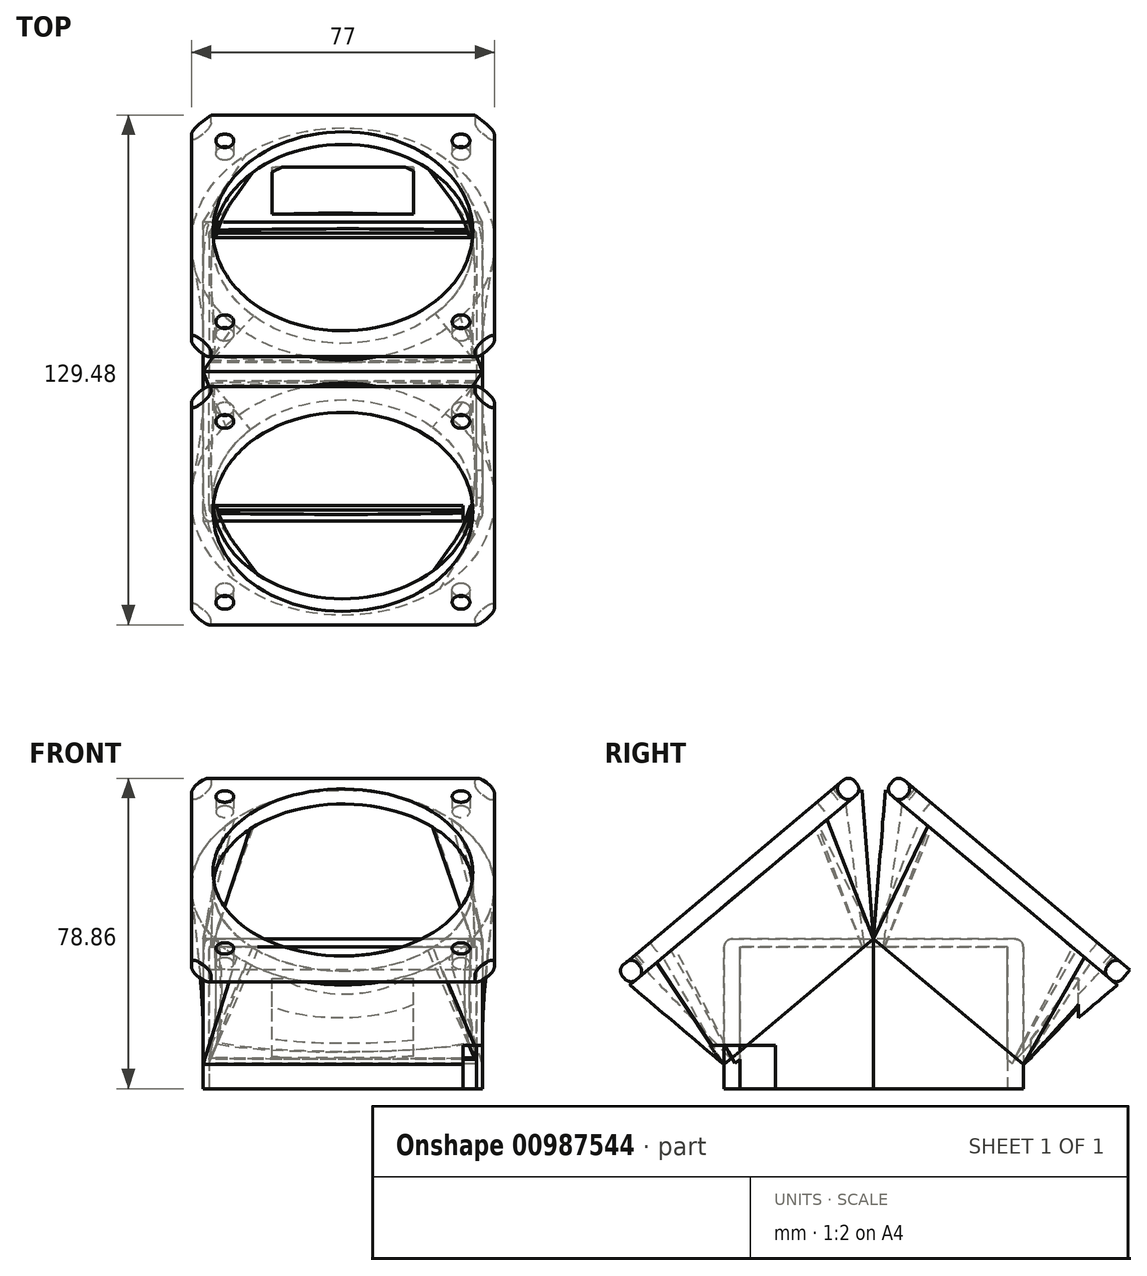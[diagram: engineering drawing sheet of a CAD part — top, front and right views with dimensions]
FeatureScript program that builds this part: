
annotation { "Feature Type Name" : "Feature", "Feature Type Description" : "" }
export const myFeature = defineFeature(function(context is Context, id is Id, definition is map)
    precondition{}
    {
        {
            var Q0;
            Q0=qCreatedBy(makeId("Front.planeOp"),FACE);
            var sketch = newSketch(context, id + "F0", { "sketchPlane" : qUnion([Q0])});
            skLineSegment(sketch, "E0.bottom", {"start": v(-34, 18) * mm, "end": v(34, 18) * mm});
            skLineSegment(sketch, "E0.top", {"start": v(-34, -18) * mm, "end": v(34, -18) * mm});
            skLineSegment(sketch, "E0.left", {"start": v(-34, 18) * mm, "end": v(-34, -18) * mm});
            skLineSegment(sketch, "E0.right", {"start": v(34, 18) * mm, "end": v(34, -18) * mm});
            skPoint(sketch, "E0.middle", {"position": v(0, 0) * mm});
            skSolve(sketch);
        }
        {
            var Q0;
            Q0=makeQuery(id+"F0.imprint","IMPRINT",FACE,{"disambiguationData":[TD([[makeQuery(id+"F0.imprint","IMPRINT",EDGE,{"derivedFrom":sQuery(id+"F0.wireOp",EDGE,"E0.bottom")}),-1.0]])]});
            extrude(context, id + "F1", {"entities" : qUnion([Q0]), "depth" : 34 * mm, "offsetDistance" : 25 * mm});
        }
        {
            var Q0;
            Q0=makeQuery(id+"F0.imprint","IMPRINT",FACE,{"disambiguationData":[TD([[makeQuery(id+"F0.imprint","IMPRINT",EDGE,{"derivedFrom":sQuery(id+"F0.wireOp",EDGE,"E0.bottom")}),-1.0]])]});
            var sketch = newSketch(context, id + "F2", { "sketchPlane" : qUnion([Q0])});
            skLineSegment(sketch, "E1", {"start": v(0, 18) * mm, "end": v(0, -18) * mm, "construction": true});
            skSolve(sketch);
        }
        {
            var Q0;
            Q0=sQuery(id+"F0.wireOp",EDGE,"E0.top");
            cPlane(context, id + "F3", {"entities" : qUnion([Q0]), "cplaneType" : CPlaneType.LINE_ANGLE, "offset" : 25 * mm, "angle" : 50 * degree, "oppositeDirection" : true, "width" : 150 * mm, "height" : 150 * mm});
        }
        {
            var Q0;
            Q0=sQuery(id+"F0.wireOp",EDGE,"E0.bottom");
            var Q1;
            Q1=qBodyType(qCreatedBy(id+"F5",EDGE),BodyType.WIRE);
            cPlane(context, id + "F4", {"entities" : qUnion([Q0, Q1]), "cplaneType" : CPlaneType.LINE_ANGLE, "offset" : 25 * mm, "angle" : 50 * degree, "oppositeDirection" : true, "width" : 150 * mm, "height" : 150 * mm});
        }
        {
            var Q0;
            Q0=qCreatedBy(id+"F4.planeOp",FACE);
            var sketch = newSketch(context, id + "F5", { "sketchPlane" : qUnion([Q0])});
            skLineSegment(sketch, "E2.bottom", {"start": v(34, -8.77) * mm, "end": v(-34, -8.77) * mm});
            skLineSegment(sketch, "E2.top", {"start": v(34, 34.4) * mm, "end": v(-34, 34.4) * mm});
            skLineSegment(sketch, "E2.left", {"start": v(34, -8.77) * mm, "end": v(34, 34.4) * mm});
            skLineSegment(sketch, "E2.right", {"start": v(-34, -8.77) * mm, "end": v(-34, 34.4) * mm});
            skSolve(sketch);
        }
        {
            var Q0;
            Q0=qCreatedBy(id+"F3.planeOp",FACE);
            cPlane(context, id + "F6", {"entities" : qUnion([Q0]), "cplaneType" : CPlaneType.OFFSET, "offset" : 60 * mm, "oppositeDirection" : true, "width" : 150 * mm, "height" : 150 * mm});
        }
        {
            var Q0;
            Q0=qCreatedBy(id+"F6.planeOp",FACE);
            var sketch = newSketch(context, id + "F7", { "sketchPlane" : qUnion([Q0])});
            skArc(sketch, "E3", {"start": v(22.98, 27.26) * mm, "mid": v(0.9, 36.56) * mm, "end": v(-21.64, 28.48) * mm});
            skArc(sketch, "E4", {"start": v(-21.64, 28.48) * mm, "mid": v(-32.97, 4.87) * mm, "end": v(-23.53, -19.57) * mm});
            skArc(sketch, "E5", {"start": v(-23.53, -19.57) * mm, "mid": v(-0.57, -29.42) * mm, "end": v(22.72, -20.36) * mm});
            skArc(sketch, "E6", {"start": v(22.72, -20.36) * mm, "mid": v(33, 3.4) * mm, "end": v(22.98, 27.26) * mm});
            skSolve(sketch);
        }
        {
            var Q0;
            Q0=qSketchRegion(id+"F5",true);
            var Q1;
            Q1=makeQuery(id+"F7.imprint","IMPRINT",FACE,{"disambiguationData":[TD([[makeQuery(id+"F7.imprint","IMPRINT",EDGE,{"derivedFrom":sQuery(id+"F7.wireOp",EDGE,"E3")}),1.0]])]});
            loft(context, id + "F8", {"sheetProfilesArray" : [{ "sheetProfileEntities" : qUnion([Q0]) }, { "sheetProfileEntities" : qUnion([Q1]) }]});
        }
        {
            var Q0;
            Q0=makeQuery(id+"F2.imprint","IMPRINT",FACE,{"disambiguationData":[TD([[makeQuery(id+"F2.imprint","IMPRINT",EDGE,{"derivedFrom":makeQuery(id+"F0.imprint","IMPRINT",EDGE,{"derivedFrom":sQuery(id+"F0.wireOp",EDGE,"E0.bottom")})}),-1.0]])]});
            var sketch = newSketch(context, id + "F9", { "sketchPlane" : qUnion([Q0])});
            skLineSegment(sketch, "E7.bottom", {"start": v(35.5, 20) * mm, "end": v(-35.5, 20) * mm});
            skLineSegment(sketch, "E7.top", {"start": v(35.5, -18) * mm, "end": v(-35.5, -18) * mm});
            skLineSegment(sketch, "E7.left", {"start": v(35.5, 20) * mm, "end": v(35.5, -18) * mm});
            skLineSegment(sketch, "E7.right", {"start": v(-35.5, 20) * mm, "end": v(-35.5, -18) * mm});
            skPoint(sketch, "E7.middle", {"position": v(0, 0) * mm});
            skSolve(sketch);
        }
        {
            var Q0;
            Q0=qSketchRegion(id+"F9",true);
            extrude(context, id + "F10", {"entities" : qUnion([Q0]), "depth" : 38 * mm, "offsetDistance" : 25 * mm});
        }
        {
            var Q0;
            Q0=sQuery(id+"F9.wireOp",EDGE,"E7.bottom");
            cPlane(context, id + "F11", {"entities" : qUnion([Q0]), "cplaneType" : CPlaneType.LINE_ANGLE, "offset" : 25 * mm, "angle" : 50 * degree, "width" : 150 * mm, "height" : 150 * mm});
        }
        {
            var Q0;
            Q0=qCreatedBy(id+"F11.planeOp",FACE);
            var sketch = newSketch(context, id + "F12", { "sketchPlane" : qUnion([Q0])});
            skLineSegment(sketch, "E8.bottom", {"start": v(-35.5, 12.86) * mm, "end": v(35.5, 12.86) * mm});
            skLineSegment(sketch, "E8.top", {"start": v(-35.5, -36.75) * mm, "end": v(35.5, -36.75) * mm});
            skLineSegment(sketch, "E8.left", {"start": v(-35.5, 12.86) * mm, "end": v(-35.5, -36.75) * mm});
            skLineSegment(sketch, "E8.right", {"start": v(35.5, 12.86) * mm, "end": v(35.5, -36.75) * mm});
            skSolve(sketch);
        }
        {
            var Q0;
            Q0=qCreatedBy(id+"F6.planeOp",FACE);
            var sketch = newSketch(context, id + "F13", { "sketchPlane" : qUnion([Q0])});
            skArc(sketch, "E9", {"start": v(-29.82, -20.78) * mm, "mid": v(-1.7, -34.9) * mm, "end": v(27.55, -23.32) * mm});
            skArc(sketch, "E10", {"start": v(27.55, -23.32) * mm, "mid": v(38.44, 5.63) * mm, "end": v(24.51, 33.26) * mm});
            skArc(sketch, "E11", {"start": v(24.51, 33.26) * mm, "mid": v(-1.62, 42.04) * mm, "end": v(-26.92, 31.1) * mm});
            skArc(sketch, "E12", {"start": v(-26.92, 31.1) * mm, "mid": v(-38.44, 5.72) * mm, "end": v(-29.82, -20.78) * mm});
            skSolve(sketch);
        }
        {
            var Q0;
            Q0=qCreatedBy(id+"F6.planeOp",FACE);
            var sketch = newSketch(context, id + "F14", { "sketchPlane" : qUnion([Q0])});
            skLineSegment(sketch, "E13.bottom", {"start": v(-38.5, -34.93) * mm, "end": v(38.5, -34.93) * mm});
            skLineSegment(sketch, "E13.top", {"start": v(-38.5, 42.07) * mm, "end": v(38.5, 42.07) * mm});
            skLineSegment(sketch, "E13.left", {"start": v(-38.5, -34.93) * mm, "end": v(-38.5, 42.07) * mm});
            skLineSegment(sketch, "E13.right", {"start": v(38.5, -34.93) * mm, "end": v(38.5, 42.07) * mm});
            skPoint(sketch, "E13.middle", {"position": v(0, 3.57) * mm});
            skSolve(sketch);
        }
        {
            var Q0;
            Q0=qCreatedBy(id+"F6.planeOp",FACE);
            var sketch = newSketch(context, id + "F15", { "sketchPlane" : qUnion([Q0])});
            skLineSegment(sketch, "E14.bottom", {"start": v(-30, -26.43) * mm, "end": v(30, -26.43) * mm, "construction": true});
            skLineSegment(sketch, "E14.top", {"start": v(-30, 33.57) * mm, "end": v(30, 33.57) * mm, "construction": true});
            skLineSegment(sketch, "E14.left", {"start": v(-30, -26.43) * mm, "end": v(-30, 33.57) * mm, "construction": true});
            skLineSegment(sketch, "E14.right", {"start": v(30, -26.43) * mm, "end": v(30, 33.57) * mm, "construction": true});
            skPoint(sketch, "E14.middle", {"position": v(0, 3.57) * mm});
            skSolve(sketch);
        }
        {
            var Q0;
            Q0=qCreatedBy(id+"F6.planeOp",FACE);
            var sketch = newSketch(context, id + "F16", { "sketchPlane" : qUnion([Q0])});
            skCircle(sketch, "E15", {"center": v(30, -26.43) * mm, "radius": 2.25 * mm});
            skCircle(sketch, "E16", {"center": v(-30, -26.43) * mm, "radius": 2.25 * mm});
            skCircle(sketch, "E17", {"center": v(-30, 33.57) * mm, "radius": 2.25 * mm});
            skCircle(sketch, "E18", {"center": v(30, 33.57) * mm, "radius": 2.25 * mm});
            skSolve(sketch);
        }
        {
            var Q0;
            Q0=makeQuery(id+"F8.opLoft","CAP_FACE",FACE,{"disambiguationData":[OSD([makeQuery(id+"F7.imprint","IMPRINT",FACE,{"disambiguationData":[TD([[makeQuery(id+"F7.imprint","IMPRINT",EDGE,{"derivedFrom":sQuery(id+"F7.wireOp",EDGE,"E3")}),1.0]])]})])],"isStart":true});
            var Q1;
            Q1=makeQuery(id+"F16.imprint","IMPRINT",FACE,{"disambiguationData":[TD([[makeQuery(id+"F16.imprint","IMPRINT",EDGE,{"derivedFrom":sQuery(id+"F16.wireOp",EDGE,"E18")}),1.0]])]});
            var Q2;
            Q2=makeQuery(id+"F16.imprint","IMPRINT",FACE,{"disambiguationData":[TD([[makeQuery(id+"F16.imprint","IMPRINT",EDGE,{"derivedFrom":sQuery(id+"F16.wireOp",EDGE,"E17")}),1.0]])]});
            var Q3;
            Q3=makeQuery(id+"F16.imprint","IMPRINT",FACE,{"disambiguationData":[TD([[makeQuery(id+"F16.imprint","IMPRINT",EDGE,{"derivedFrom":sQuery(id+"F16.wireOp",EDGE,"E16")}),1.0]])]});
            var Q4;
            Q4=makeQuery(id+"F16.imprint","IMPRINT",FACE,{"disambiguationData":[TD([[makeQuery(id+"F16.imprint","IMPRINT",EDGE,{"derivedFrom":sQuery(id+"F16.wireOp",EDGE,"E15")}),1.0]])]});
            extrude(context, id + "F17", {"entities" : qUnion([Q0, Q1, Q2, Q3, Q4]), "depth" : 5 * mm, "offsetDistance" : 25 * mm});
        }
        {
            var Q0;
            Q0=makeQuery(id+"F12.imprint","IMPRINT",FACE,{"disambiguationData":[TD([[makeQuery(id+"F12.imprint","IMPRINT",EDGE,{"derivedFrom":sQuery(id+"F12.wireOp",EDGE,"E8.bottom")}),-1.0]])]});
            var Q1;
            Q1=qSketchRegion(id+"F13",true);
            loft(context, id + "F18", {"sheetProfilesArray" : [{ "sheetProfileEntities" : qUnion([Q0]) }, { "sheetProfileEntities" : qUnion([Q1]) }]});
        }
        {
            var Q0;
            Q0=makeQuery(id+"F14.imprint","IMPRINT",FACE,{"disambiguationData":[TD([[makeQuery(id+"F14.imprint","IMPRINT",EDGE,{"derivedFrom":sQuery(id+"F14.wireOp",EDGE,"E13.bottom")}),1.0]])]});
            extrude(context, id + "F19", {"entities" : qUnion([Q0]), "oppositeDirection" : true, "depth" : 5 * mm, "offsetDistance" : 25 * mm});
        }
        {
            var Q0;
            Q0=makeQuery(id+"F17.opExtrude","SWEPT_BODY",BODY,{"disambiguationData":[OSD([sQuery(id+"F16.wireOp",EDGE,"E18")])]});
            var Q1;
            Q1=makeQuery(id+"F17.opExtrude","SWEPT_BODY",BODY,{"disambiguationData":[OSD([sQuery(id+"F16.wireOp",EDGE,"E17")])]});
            var Q2;
            Q2=makeQuery(id+"F17.opExtrude","SWEPT_BODY",BODY,{"disambiguationData":[OSD([sQuery(id+"F16.wireOp",EDGE,"E16")])]});
            var Q3;
            Q3=makeQuery(id+"F17.opExtrude","SWEPT_BODY",BODY,{"disambiguationData":[OSD([sQuery(id+"F16.wireOp",EDGE,"E15")])]});
            var Q4;
            Q4=makeQuery(id+"F17.opExtrude","SWEPT_BODY",BODY,{"disambiguationData":[OSD([makeQuery(id+"F7.imprint","IMPRINT",FACE,{"disambiguationData":[TD([[makeQuery(id+"F7.imprint","IMPRINT",EDGE,{"derivedFrom":sQuery(id+"F7.wireOp",EDGE,"E3")}),1.0]])]})])]});
            var Q5;
            Q5=makeQuery(id+"F8.opLoft","SWEPT_BODY",BODY,{"disambiguationData":[OSD([makeQuery(id+"F5.imprint","IMPRINT",FACE,{"disambiguationData":[TD([[makeQuery(id+"F5.imprint","IMPRINT",EDGE,{"derivedFrom":sQuery(id+"F5.wireOp",EDGE,"sHmJ6Bm4-Lffu-TfJG-ELbj-xKBSEGzgKOYK.bottom")}),-1.0]])]}),makeQuery(id+"F7.imprint","IMPRINT",FACE,{"disambiguationData":[TD([[makeQuery(id+"F7.imprint","IMPRINT",EDGE,{"derivedFrom":sQuery(id+"F7.wireOp",EDGE,"E3")}),1.0]])]})])]});
            var Q6;
            Q6=makeQuery(id+"F1.opExtrude","SWEPT_BODY",BODY,{"disambiguationData":[OSD([sQuery(id+"F0.wireOp",EDGE,"E0.bottom"),sQuery(id+"F0.wireOp",EDGE,"E0.top"),sQuery(id+"F0.wireOp",EDGE,"E0.left"),sQuery(id+"F0.wireOp",EDGE,"E0.right")])]});
            var Q7;
            Q7=makeQuery(id+"F10.opExtrude","SWEPT_BODY",BODY,{"disambiguationData":[OSD([sQuery(id+"F9.wireOp",EDGE,"E7.bottom"),sQuery(id+"F9.wireOp",EDGE,"E7.top"),sQuery(id+"F9.wireOp",EDGE,"E7.left"),sQuery(id+"F9.wireOp",EDGE,"E7.right")])]});
            var Q8;
            Q8=makeQuery(id+"F18.opLoft","SWEPT_BODY",BODY,{"disambiguationData":[OSD([makeQuery(id+"F12.imprint","IMPRINT",FACE,{"disambiguationData":[TD([[makeQuery(id+"F12.imprint","IMPRINT",EDGE,{"derivedFrom":sQuery(id+"F12.wireOp",EDGE,"E8.bottom")}),-1.0]])]}),makeQuery(id+"F13.imprint","IMPRINT",FACE,{"disambiguationData":[TD([[makeQuery(id+"F13.imprint","IMPRINT",EDGE,{"derivedFrom":sQuery(id+"F13.wireOp",EDGE,"q23MTACi-eoCC-Vc5T-UU1i-hVDggLDGJppy")}),1.0]])]})])]});
            var Q9;
            Q9=makeQuery(id+"F19.opExtrude","SWEPT_BODY",BODY,{"disambiguationData":[OSD([sQuery(id+"F14.wireOp",EDGE,"E13.bottom"),sQuery(id+"F14.wireOp",EDGE,"E13.top"),sQuery(id+"F14.wireOp",EDGE,"E13.left"),sQuery(id+"F14.wireOp",EDGE,"E13.right")])]});
            booleanBodies(context, id + "F20", {"operationType" : BooleanOperationType.SUBTRACTION, "tools" : qUnion([Q0, Q1, Q2, Q3, Q4, Q5, Q6]), "targets" : qUnion([Q7, Q8, Q9])});
        }
        {
            var Q0;
            Q0=makeQuery(id+"F10.opExtrude","SWEPT_BODY",BODY,{"disambiguationData":[OSD([sQuery(id+"F9.wireOp",EDGE,"E7.bottom"),sQuery(id+"F9.wireOp",EDGE,"E7.top"),sQuery(id+"F9.wireOp",EDGE,"E7.left"),sQuery(id+"F9.wireOp",EDGE,"E7.right")])]});
            var Q1;
            Q1=sQuery(id+"F2.wireOp",EDGE,"E1");
            transform(context, id + "F21", {"entities" : qUnion([Q0]), "transformType" : TransformType.ROTATION, "transformAxis" : qUnion([Q1]), "angle" : 180 * degree, "makeCopy" : true});
        }
        {
            var Q0;
            Q0=makeQuery(id+"F18.opLoft","SWEPT_BODY",BODY,{"disambiguationData":[OSD([makeQuery(id+"F12.imprint","IMPRINT",FACE,{"disambiguationData":[TD([[makeQuery(id+"F12.imprint","IMPRINT",EDGE,{"derivedFrom":sQuery(id+"F12.wireOp",EDGE,"E8.bottom")}),-1.0]])]}),makeQuery(id+"F13.imprint","IMPRINT",FACE,{"disambiguationData":[TD([[makeQuery(id+"F13.imprint","IMPRINT",EDGE,{"derivedFrom":sQuery(id+"F13.wireOp",EDGE,"q23MTACi-eoCC-Vc5T-UU1i-hVDggLDGJppy")}),1.0]])]})])]});
            var Q1;
            Q1=sQuery(id+"F2.wireOp",EDGE,"E1");
            transform(context, id + "F22", {"entities" : qUnion([Q0]), "transformType" : TransformType.ROTATION, "transformAxis" : qUnion([Q1]), "angle" : 180 * degree, "makeCopy" : true});
        }
        {
            var Q0;
            Q0=makeQuery(id+"F19.opExtrude","SWEPT_BODY",BODY,{"disambiguationData":[OSD([sQuery(id+"F14.wireOp",EDGE,"E13.bottom"),sQuery(id+"F14.wireOp",EDGE,"E13.top"),sQuery(id+"F14.wireOp",EDGE,"E13.left"),sQuery(id+"F14.wireOp",EDGE,"E13.right")])]});
            var Q1;
            Q1=sQuery(id+"F2.wireOp",EDGE,"E1");
            transform(context, id + "F23", {"entities" : qUnion([Q0]), "transformType" : TransformType.ROTATION, "transformAxis" : qUnion([Q1]), "angle" : 180 * degree, "makeCopy" : true});
        }
        {
            var Q0;
            Q0=makeQuery(id+"F19.opExtrude","SWEPT_EDGE",EDGE,{"disambiguationData":[OSD([sQuery(id+"F14.wireOp",EDGE,"E13.top"),sQuery(id+"F14.wireOp",EDGE,"E13.right")])]});
            var Q1;
            Q1=makeQuery(id+"F19.opExtrude","SWEPT_EDGE",EDGE,{"disambiguationData":[OSD([sQuery(id+"F14.wireOp",EDGE,"E13.top"),sQuery(id+"F14.wireOp",EDGE,"E13.left")])]});
            var Q2;
            Q2=makeQuery(id+"F19.opExtrude","SWEPT_EDGE",EDGE,{"disambiguationData":[OSD([sQuery(id+"F14.wireOp",EDGE,"E13.bottom"),sQuery(id+"F14.wireOp",EDGE,"E13.right")])]});
            var Q3;
            Q3=makeQuery(id+"F19.opExtrude","SWEPT_EDGE",EDGE,{"disambiguationData":[OSD([sQuery(id+"F14.wireOp",EDGE,"E13.bottom"),sQuery(id+"F14.wireOp",EDGE,"E13.left")])]});
            var Q4;
            Q4=makeQuery(id+"F23.opPattern","COPY",EDGE,{"derivedFrom":makeQuery(id+"F19.opExtrude","SWEPT_EDGE",EDGE,{"disambiguationData":[OSD([sQuery(id+"F14.wireOp",EDGE,"E13.bottom"),sQuery(id+"F14.wireOp",EDGE,"E13.right")])]}),"instanceName":"1"});
            var Q5;
            Q5=makeQuery(id+"F23.opPattern","COPY",EDGE,{"derivedFrom":makeQuery(id+"F19.opExtrude","SWEPT_EDGE",EDGE,{"disambiguationData":[OSD([sQuery(id+"F14.wireOp",EDGE,"E13.bottom"),sQuery(id+"F14.wireOp",EDGE,"E13.left")])]}),"instanceName":"1"});
            var Q6;
            Q6=makeQuery(id+"F23.opPattern","COPY",EDGE,{"derivedFrom":makeQuery(id+"F19.opExtrude","SWEPT_EDGE",EDGE,{"disambiguationData":[OSD([sQuery(id+"F14.wireOp",EDGE,"E13.top"),sQuery(id+"F14.wireOp",EDGE,"E13.left")])]}),"instanceName":"1"});
            var Q7;
            Q7=makeQuery(id+"F23.opPattern","COPY",EDGE,{"derivedFrom":makeQuery(id+"F19.opExtrude","SWEPT_EDGE",EDGE,{"disambiguationData":[OSD([sQuery(id+"F14.wireOp",EDGE,"E13.top"),sQuery(id+"F14.wireOp",EDGE,"E13.right")])]}),"instanceName":"1"});
            chamfer(context, id + "F24", {"entities" : qUnion([Q0, Q1, Q2, Q3, Q4, Q5, Q6, Q7]), "width" : 5 * mm, "tangentPropagation" : true});
        }
        {
            var Q0;
            Q0=makeQuery(id+"F19.opExtrude","CAP_EDGE",EDGE,{"disambiguationData":[OSD([sQuery(id+"F14.wireOp",EDGE,"E13.left")])],"isStart":false});
            var Q1;
            Q1=makeQuery(id+"F19.opExtrude","CAP_EDGE",EDGE,{"disambiguationData":[OSD([sQuery(id+"F14.wireOp",EDGE,"E13.top")])],"isStart":false});
            var Q2;
            Q2=makeQuery(id+"F19.opExtrude","CAP_EDGE",EDGE,{"disambiguationData":[OSD([sQuery(id+"F14.wireOp",EDGE,"E13.right")])],"isStart":false});
            var Q3;
            Q3=makeQuery(id+"F19.opExtrude","CAP_EDGE",EDGE,{"disambiguationData":[OSD([sQuery(id+"F14.wireOp",EDGE,"E13.bottom")])],"isStart":false});
            var Q4;
            Q4=makeQuery(id+"F19.opExtrude","CAP_EDGE",EDGE,{"disambiguationData":[OSD([sQuery(id+"F14.wireOp",EDGE,"E13.left")])],"isStart":true});
            var Q5;
            Q5=makeQuery(id+"F19.opExtrude","CAP_EDGE",EDGE,{"disambiguationData":[OSD([sQuery(id+"F14.wireOp",EDGE,"E13.bottom")])],"isStart":true});
            var Q6;
            Q6=makeQuery(id+"F19.opExtrude","CAP_EDGE",EDGE,{"disambiguationData":[OSD([sQuery(id+"F14.wireOp",EDGE,"E13.right")])],"isStart":true});
            var Q7;
            Q7=makeQuery(id+"F19.opExtrude","CAP_EDGE",EDGE,{"disambiguationData":[OSD([sQuery(id+"F14.wireOp",EDGE,"E13.top")])],"isStart":true});
            var Q8;
            Q8=makeQuery(id+"F10.opExtrude","CAP_EDGE",EDGE,{"disambiguationData":[OSD([sQuery(id+"F9.wireOp",EDGE,"E7.right")])],"isStart":false});
            var Q9;
            {var subQ0=sQuery(id+"F9.wireOp",EDGE,"E7.bottom");var subQ1=sQuery(id+"F9.wireOp",EDGE,"E7.right");Q9=makeQuery(id+"F20.opBoolean","SPLIT",EDGE,{"disambiguationData":[TD([makeQuery(id+"F10.opExtrude","SWEPT_FACE",FACE,{"disambiguationData":[OSD([subQ1])]})])],"derivedFrom":makeQuery(id+"F10.opExtrude","CAP_EDGE",EDGE,{"disambiguationData":[OSD([subQ0])],"isStart":false})});}
            var Q10;
            Q10=makeQuery(id+"F10.opExtrude","SWEPT_EDGE",EDGE,{"disambiguationData":[OSD([sQuery(id+"F9.wireOp",EDGE,"E7.bottom"),sQuery(id+"F9.wireOp",EDGE,"E7.right")])]});
            var Q11;
            Q11=makeQuery(id+"F10.opExtrude","CAP_EDGE",EDGE,{"disambiguationData":[OSD([sQuery(id+"F9.wireOp",EDGE,"E7.left")])],"isStart":false});
            var Q12;
            Q12=makeQuery(id+"F10.opExtrude","SWEPT_EDGE",EDGE,{"disambiguationData":[OSD([sQuery(id+"F9.wireOp",EDGE,"E7.bottom"),sQuery(id+"F9.wireOp",EDGE,"E7.left")])]});
            var Q13;
            {var subQ0=sQuery(id+"F9.wireOp",EDGE,"E7.bottom");var subQ1=sQuery(id+"F9.wireOp",EDGE,"E7.left");Q13=makeQuery(id+"F20.opBoolean","SPLIT",EDGE,{"disambiguationData":[TD([makeQuery(id+"F10.opExtrude","SWEPT_FACE",FACE,{"disambiguationData":[OSD([subQ1])]})])],"derivedFrom":makeQuery(id+"F10.opExtrude","CAP_EDGE",EDGE,{"disambiguationData":[OSD([subQ0])],"isStart":false})});}
            var Q14;
            Q14=makeQuery(id+"F21.opPattern","COPY",EDGE,{"derivedFrom":makeQuery(id+"F10.opExtrude","SWEPT_EDGE",EDGE,{"disambiguationData":[OSD([sQuery(id+"F9.wireOp",EDGE,"E7.bottom"),sQuery(id+"F9.wireOp",EDGE,"E7.right")])]}),"instanceName":"1"});
            var Q15;
            {var subQ0=sQuery(id+"F9.wireOp",EDGE,"E7.bottom");var subQ1=sQuery(id+"F9.wireOp",EDGE,"E7.right");Q15=makeQuery(id+"F21.opPattern","COPY",EDGE,{"derivedFrom":makeQuery(id+"F20.opBoolean","SPLIT",EDGE,{"disambiguationData":[TD([makeQuery(id+"F10.opExtrude","SWEPT_FACE",FACE,{"disambiguationData":[OSD([subQ1])]})])],"derivedFrom":makeQuery(id+"F10.opExtrude","CAP_EDGE",EDGE,{"disambiguationData":[OSD([subQ0])],"isStart":false})}),"instanceName":"1"});}
            var Q16;
            Q16=makeQuery(id+"F21.opPattern","COPY",EDGE,{"derivedFrom":makeQuery(id+"F10.opExtrude","CAP_EDGE",EDGE,{"disambiguationData":[OSD([sQuery(id+"F9.wireOp",EDGE,"E7.right")])],"isStart":false}),"instanceName":"1"});
            var Q17;
            Q17=makeQuery(id+"F23.opPattern","COPY",EDGE,{"derivedFrom":makeQuery(id+"F19.opExtrude","CAP_EDGE",EDGE,{"disambiguationData":[OSD([sQuery(id+"F14.wireOp",EDGE,"E13.right")])],"isStart":false}),"instanceName":"1"});
            var Q18;
            Q18=makeQuery(id+"F23.opPattern","COPY",EDGE,{"derivedFrom":makeQuery(id+"F19.opExtrude","CAP_EDGE",EDGE,{"disambiguationData":[OSD([sQuery(id+"F14.wireOp",EDGE,"E13.right")])],"isStart":true}),"instanceName":"1"});
            var Q19;
            Q19=makeQuery(id+"F23.opPattern","COPY",EDGE,{"derivedFrom":makeQuery(id+"F19.opExtrude","CAP_EDGE",EDGE,{"disambiguationData":[OSD([sQuery(id+"F14.wireOp",EDGE,"E13.top")])],"isStart":true}),"instanceName":"1"});
            var Q20;
            Q20=makeQuery(id+"F23.opPattern","COPY",EDGE,{"derivedFrom":makeQuery(id+"F19.opExtrude","CAP_EDGE",EDGE,{"disambiguationData":[OSD([sQuery(id+"F14.wireOp",EDGE,"E13.bottom")])],"isStart":true}),"instanceName":"1"});
            var Q21;
            Q21=makeQuery(id+"F23.opPattern","COPY",EDGE,{"derivedFrom":makeQuery(id+"F19.opExtrude","CAP_EDGE",EDGE,{"disambiguationData":[OSD([sQuery(id+"F14.wireOp",EDGE,"E13.bottom")])],"isStart":false}),"instanceName":"1"});
            var Q22;
            Q22=makeQuery(id+"F23.opPattern","COPY",EDGE,{"derivedFrom":makeQuery(id+"F19.opExtrude","CAP_EDGE",EDGE,{"disambiguationData":[OSD([sQuery(id+"F14.wireOp",EDGE,"E13.left")])],"isStart":false}),"instanceName":"1"});
            var Q23;
            Q23=makeQuery(id+"F23.opPattern","COPY",EDGE,{"derivedFrom":makeQuery(id+"F19.opExtrude","CAP_EDGE",EDGE,{"disambiguationData":[OSD([sQuery(id+"F14.wireOp",EDGE,"E13.left")])],"isStart":true}),"instanceName":"1"});
            var Q24;
            Q24=makeQuery(id+"F21.opPattern","COPY",EDGE,{"derivedFrom":makeQuery(id+"F10.opExtrude","CAP_EDGE",EDGE,{"disambiguationData":[OSD([sQuery(id+"F9.wireOp",EDGE,"E7.left")])],"isStart":false}),"instanceName":"1"});
            var Q25;
            {var subQ0=sQuery(id+"F9.wireOp",EDGE,"E7.bottom");var subQ1=sQuery(id+"F9.wireOp",EDGE,"E7.left");Q25=makeQuery(id+"F21.opPattern","COPY",EDGE,{"derivedFrom":makeQuery(id+"F20.opBoolean","SPLIT",EDGE,{"disambiguationData":[TD([makeQuery(id+"F10.opExtrude","SWEPT_FACE",FACE,{"disambiguationData":[OSD([subQ1])]})])],"derivedFrom":makeQuery(id+"F10.opExtrude","CAP_EDGE",EDGE,{"disambiguationData":[OSD([subQ0])],"isStart":false})}),"instanceName":"1"});}
            var Q26;
            Q26=makeQuery(id+"F21.opPattern","COPY",EDGE,{"derivedFrom":makeQuery(id+"F10.opExtrude","SWEPT_EDGE",EDGE,{"disambiguationData":[OSD([sQuery(id+"F9.wireOp",EDGE,"E7.bottom"),sQuery(id+"F9.wireOp",EDGE,"E7.left")])]}),"instanceName":"1"});
            fillet(context, id + "F25", {"entities" : qUnion([Q0, Q1, Q2, Q3, Q4, Q5, Q6, Q7, Q8, Q9, Q10, Q11, Q12, Q13, Q14, Q15, Q16, Q17, Q18, Q19, Q20, Q21, Q22, Q23, Q24, Q25, Q26]), "radius" : 2 * mm, "tangentPropagation" : true, "allowEdgeOverflow" : false});
        }
        {
            var Q0;
            Q0=makeQuery(id+"F10.opExtrude","SWEPT_FACE",FACE,{"disambiguationData":[OSD([sQuery(id+"F9.wireOp",EDGE,"E7.left")])]});
            var sketch = newSketch(context, id + "F26", { "sketchPlane" : qUnion([Q0])});
            skLineSegment(sketch, "E19.bottom", {"start": v(-25, -19) * mm, "end": v(-45, -19) * mm});
            skLineSegment(sketch, "E19.top", {"start": v(-25, -7) * mm, "end": v(-45, -7) * mm});
            skLineSegment(sketch, "E19.left", {"start": v(-25, -19) * mm, "end": v(-25, -7) * mm});
            skLineSegment(sketch, "E19.right", {"start": v(-45, -19) * mm, "end": v(-45, -7) * mm});
            skSolve(sketch);
        }
        {
            var Q0;
            Q0=qSketchRegion(id+"F26",true);
            extrude(context, id + "F27", {"entities" : qUnion([Q0]), "oppositeDirection" : true, "depth" : 5 * mm, "offsetDistance" : 25 * mm});
        }
        {
            var Q0;
            Q0=makeQuery(id+"F27.opExtrude","SWEPT_BODY",BODY,{"disambiguationData":[OSD([sQuery(id+"F26.wireOp",EDGE,"E19.bottom"),sQuery(id+"F26.wireOp",EDGE,"E19.top"),sQuery(id+"F26.wireOp",EDGE,"E19.left"),sQuery(id+"F26.wireOp",EDGE,"E19.right")])]});
            var Q1;
            Q1=makeQuery(id+"F10.opExtrude","SWEPT_BODY",BODY,{"disambiguationData":[OSD([sQuery(id+"F9.wireOp",EDGE,"E7.bottom"),sQuery(id+"F9.wireOp",EDGE,"E7.top"),sQuery(id+"F9.wireOp",EDGE,"E7.left"),sQuery(id+"F9.wireOp",EDGE,"E7.right")])]});
            var Q2;
            Q2=makeQuery(id+"F18.opLoft","SWEPT_BODY",BODY,{"disambiguationData":[OSD([makeQuery(id+"F12.imprint","IMPRINT",FACE,{"disambiguationData":[TD([[makeQuery(id+"F12.imprint","IMPRINT",EDGE,{"derivedFrom":sQuery(id+"F12.wireOp",EDGE,"E8.bottom")}),-1.0]])]}),makeQuery(id+"F13.imprint","IMPRINT",FACE,{"disambiguationData":[TD([[makeQuery(id+"F13.imprint","IMPRINT",EDGE,{"derivedFrom":sQuery(id+"F13.wireOp",EDGE,"q23MTACi-eoCC-Vc5T-UU1i-hVDggLDGJppy")}),1.0]])]})])]});
            booleanBodies(context, id + "F28", {"operationType" : BooleanOperationType.SUBTRACTION, "tools" : qUnion([Q0]), "targets" : qUnion([Q1, Q2])});
        }
        {
            var Q0;
            Q0=qCreatedBy(makeId("Top.planeOp"),FACE);
            var sketch = newSketch(context, id + "F29", { "sketchPlane" : qUnion([Q0])});
            skLineSegment(sketch, "E20.bottom", {"start": v(-18, 52) * mm, "end": v(18, 52) * mm});
            skLineSegment(sketch, "E20.top", {"start": v(-18, 40) * mm, "end": v(18, 40) * mm});
            skLineSegment(sketch, "E20.left", {"start": v(-18, 52) * mm, "end": v(-18, 40) * mm});
            skLineSegment(sketch, "E20.right", {"start": v(18, 52) * mm, "end": v(18, 40) * mm});
            skPoint(sketch, "E20.middle", {"position": v(0, 46) * mm});
            skSolve(sketch);
        }
        {
            var Q0;
            Q0 = qSketchRegion(id + "F29", true);
            extrude(context, id + "F30", {"entities" : qUnion([Q0]), "endBound" : BoundingType.SYMMETRIC, "oppositeDirection" : true, "depth" : 20 * mm, "offsetDistance" : 25 * mm});
        }
        {
            var Q0;
            Q0=makeQuery(id+"F30.opExtrude","SWEPT_BODY",BODY,{"disambiguationData":[OSD([sQuery(id+"F29.wireOp",EDGE,"E20.bottom"),sQuery(id+"F29.wireOp",EDGE,"E20.top"),sQuery(id+"F29.wireOp",EDGE,"E20.left"),sQuery(id+"F29.wireOp",EDGE,"E20.right")])]});
            var Q1;
            Q1=makeQuery(id+"F23.opPattern","COPY",BODY,{"derivedFrom":makeQuery(id+"F19.opExtrude","SWEPT_BODY",BODY,{"disambiguationData":[OSD([sQuery(id+"F14.wireOp",EDGE,"E13.bottom"),sQuery(id+"F14.wireOp",EDGE,"E13.top"),sQuery(id+"F14.wireOp",EDGE,"E13.left"),sQuery(id+"F14.wireOp",EDGE,"E13.right")])]}),"instanceName":"1"});
            var Q2;
            Q2=makeQuery(id+"F21.opPattern","COPY",BODY,{"derivedFrom":makeQuery(id+"F10.opExtrude","SWEPT_BODY",BODY,{"disambiguationData":[OSD([sQuery(id+"F9.wireOp",EDGE,"E7.bottom"),sQuery(id+"F9.wireOp",EDGE,"E7.top"),sQuery(id+"F9.wireOp",EDGE,"E7.left"),sQuery(id+"F9.wireOp",EDGE,"E7.right")])]}),"instanceName":"1"});
            var Q3;
            Q3=makeQuery(id+"F22.opPattern","COPY",BODY,{"derivedFrom":makeQuery(id+"F18.opLoft","SWEPT_BODY",BODY,{"disambiguationData":[OSD([makeQuery(id+"F12.imprint","IMPRINT",FACE,{"disambiguationData":[TD([[makeQuery(id+"F12.imprint","IMPRINT",EDGE,{"derivedFrom":sQuery(id+"F12.wireOp",EDGE,"E8.bottom")}),-1.0]])]}),makeQuery(id+"F13.imprint","IMPRINT",FACE,{"disambiguationData":[TD([[makeQuery(id+"F13.imprint","IMPRINT",EDGE,{"derivedFrom":sQuery(id+"F13.wireOp",EDGE,"E9")}),1.0]])]})])]}),"instanceName":"1"});
            booleanBodies(context, id + "F31", {"operationType" : BooleanOperationType.SUBTRACTION, "tools" : qUnion([Q0]), "targets" : qUnion([Q1, Q2, Q3])});
        }
    });
